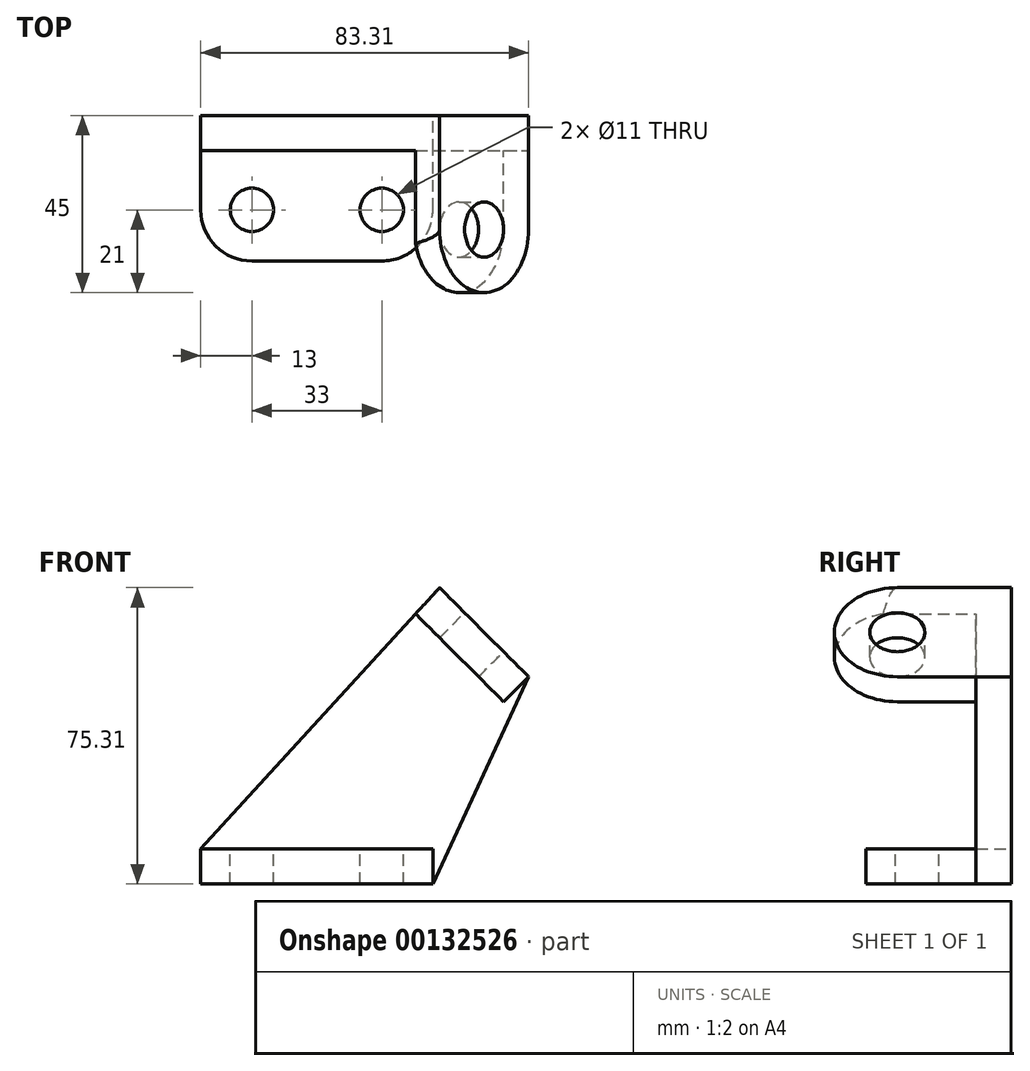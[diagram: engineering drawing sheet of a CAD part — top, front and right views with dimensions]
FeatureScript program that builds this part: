
annotation { "Feature Type Name" : "Feature", "Feature Type Description" : "" }
export const myFeature = defineFeature(function(context is Context, id is Id, definition is map)
    precondition{}
    {
        {
            var Q0;
            Q0=qCreatedBy(makeId("Front.planeOp"),FACE);
            var sketch = newSketch(context, id + "F0", { "sketchPlane" : qUnion([Q0])});
            skLineSegment(sketch, "E0.bottom", {"start": v(0, 0) * mm, "end": v(59, 0) * mm});
            skLineSegment(sketch, "E0.top", {"start": v(0, 9) * mm, "end": v(59, 9) * mm});
            skLineSegment(sketch, "E0.left", {"start": v(0, 0) * mm, "end": v(0, 9) * mm});
            skLineSegment(sketch, "E0.right", {"start": v(59, 0) * mm, "end": v(59, 9) * mm});
            skSolve(sketch);
        }
        {
            var Q0;
            Q0=makeQuery(id+"F0.imprint","IMPRINT",FACE,{"disambiguationData":[TD([[makeQuery(id+"F0.imprint","IMPRINT",EDGE,{"derivedFrom":sQuery(id+"F0.wireOp",EDGE,"E0.bottom")}),1.0]])]});
            extrude(context, id + "F1", {"entities" : qUnion([Q0]), "depth" : 37 * mm});
        }
        {
            var Q0;
            Q0=makeQuery(id+"F1.opExtrude","SWEPT_FACE",FACE,{"disambiguationData":[OSD([sQuery(id+"F0.wireOp",EDGE,"E0.top")])]});
            var sketch = newSketch(context, id + "F2", { "sketchPlane" : qUnion([Q0])});
            skCircle(sketch, "E1", {"center": v(46, -24) * mm, "radius": 5.5 * mm});
            skCircle(sketch, "E2", {"center": v(13, -24) * mm, "radius": 5.5 * mm});
            skSolve(sketch);
        }
        {
            var Q0;
            Q0 = qSketchRegion(id + "F2", true);
            var Q1;
            Q1=makeQuery(id+"F2.imprint","IMPRINT",FACE,{"disambiguationData":[TD([[makeQuery(id+"F2.imprint","IMPRINT",EDGE,{"derivedFrom":sQuery(id+"F2.wireOp",EDGE,"E2")}),1.0]])]});
            extrude(context, id + "F3", {"entities" : qUnion([Q0, Q1]), "operationType" : NewBodyOperationType.REMOVE, "oppositeDirection" : true, "depth" : 25 * mm});
        }
        {
            var Q0;
            Q0=makeQuery(id+"F1.opExtrude","CAP_FACE",FACE,{"disambiguationData":[OSD([sQuery(id+"F0.wireOp",EDGE,"E0.bottom"),sQuery(id+"F0.wireOp",EDGE,"E0.top"),sQuery(id+"F0.wireOp",EDGE,"E0.left"),sQuery(id+"F0.wireOp",EDGE,"E0.right")])],"isStart":true});
            var sketch = newSketch(context, id + "F4", { "sketchPlane" : qUnion([Q0])});
            skLineSegment(sketch, "E3", {"start": v(-59, 0) * mm, "end": v(-72, 0) * mm, "construction": true});
            skLineSegment(sketch, "E4", {"start": v(-72, 0) * mm, "end": v(-72, 80.83) * mm, "construction": true});
            skLineSegment(sketch, "E5", {"start": v(-61.08, 64) * mm, "end": v(-84.47, 64) * mm, "construction": true});
            skCircle(sketch, "E6", {"center": v(-72, 64) * mm, "radius": 1.23 * mm, "construction": true});
            skLineSegment(sketch, "E7", {"start": v(-72, 64) * mm, "end": v(-83.31, 52.69) * mm});
            skLineSegment(sketch, "E8", {"start": v(-72, 64) * mm, "end": v(-60.69, 75.31) * mm});
            skLineSegment(sketch, "E9", {"start": v(-59, 0) * mm, "end": v(-83.31, 52.69) * mm});
            skLineSegment(sketch, "E10", {"start": v(0, 9) * mm, "end": v(-60.69, 75.31) * mm});
            skLineSegment(sketch, "E11", {"start": v(-60.69, 75.31) * mm, "end": v(-54.61, 68.67) * mm});
            skLineSegment(sketch, "E12", {"start": v(-83.31, 52.69) * mm, "end": v(-77.24, 46.05) * mm});
            skLineSegment(sketch, "E13", {"start": v(-54.61, 68.67) * mm, "end": v(-77.24, 46.05) * mm});
            skSolve(sketch);
        }
        {
            var Q0;
            Q0=makeQuery(id+"F4.imprint","IMPRINT",FACE,{"disambiguationData":[TD([[makeQuery(id+"F4.imprint","IMPRINT",EDGE,{"derivedFrom":sQuery(id+"F4.wireOp",EDGE,"E9")}),-1.0]])]});
            extrude(context, id + "F5", {"entities" : qUnion([Q0]), "operationType" : NewBodyOperationType.ADD, "oppositeDirection" : true, "depth" : 9 * mm});
        }
        {
            var Q0;
            Q0=makeQuery(id+"F4.imprint","IMPRINT",FACE,{"disambiguationData":[TD([[makeQuery(id+"F4.imprint","IMPRINT",EDGE,{"derivedFrom":sQuery(id+"F4.wireOp",EDGE,"E7")}),1.0]])]});
            extrude(context, id + "F6", {"entities" : qUnion([Q0]), "operationType" : NewBodyOperationType.ADD, "oppositeDirection" : true, "depth" : 45 * mm});
        }
        {
            var Q0;
            Q0=makeQuery(id+"F6.opExtrude","SWEPT_FACE",FACE,{"disambiguationData":[OSD([sQuery(id+"F4.wireOp",EDGE,"E7"),sQuery(id+"F4.wireOp",EDGE,"E8")])]});
            var sketch = newSketch(context, id + "F7", { "sketchPlane" : qUnion([Q0])});
            skCircle(sketch, "E14", {"center": v(-29, -5.66) * mm, "radius": 7 * mm});
            skPoint(sketch, "E14.centerSnap0", {"position": v(0, -5.66) * mm});
            skArc(sketch, "E15", {"start": v(-29, 10.34) * mm, "mid": v(-45, -5.66) * mm, "end": v(-29, -21.66) * mm});
            skLineSegment(sketch, "E16", {"start": v(-29, -21.66) * mm, "end": v(0, -21.66) * mm});
            skLineSegment(sketch, "E17", {"start": v(-29, 10.34) * mm, "end": v(0, 10.34) * mm});
            skLineSegment(sketch, "E18", {"start": v(0, -21.66) * mm, "end": v(0, 10.34) * mm});
            skSolve(sketch);
        }
        {
            var Q0;
            Q0=makeQuery(id+"F7.imprint","IMPRINT",FACE,{"disambiguationData":[TD([[makeQuery(id+"F7.imprint","IMPRINT",EDGE,{"derivedFrom":sQuery(id+"F7.wireOp",EDGE,"E14")}),1.0]])]});
            var Q1;
            {var subQ0=sQuery(id+"F7.wireOp",EDGE,"E15");var subQ1=sQuery(id+"F4.wireOp",EDGE,"E8");var subQ2=makeQuery(id+"F6.opExtrude","SWEPT_EDGE",EDGE,{"disambiguationData":[OSD([subQ1,sQuery(id+"F4.wireOp",EDGE,"E11")])]});var subQ3=makeQuery(id+"F7.imprint","INTERSECT",VERTEX,{"derivedFrom":[subQ2,subQ0]});Q1=makeQuery(id+"F7.imprint","IMPRINT",FACE,{"disambiguationData":[TD([[makeQuery(id+"F7.imprint","IMPRINT",EDGE,{"disambiguationData":[TD([[subQ3,-1.0]])],"derivedFrom":subQ0}),-1.0]])]});}
            var Q2;
            {var subQ0=sQuery(id+"F7.wireOp",EDGE,"E15");var subQ1=sQuery(id+"F4.wireOp",EDGE,"E7");var subQ4=makeQuery(id+"F6.opExtrude","CAP_EDGE",EDGE,{"disambiguationData":[OSD([subQ1,sQuery(id+"F4.wireOp",EDGE,"E8")])],"isStart":false});var subQ5=makeQuery(id+"F7.imprint","INTERSECT",VERTEX,{"derivedFrom":[subQ4,subQ0]});Q2=makeQuery(id+"F7.imprint","IMPRINT",FACE,{"disambiguationData":[TD([[makeQuery(id+"F7.imprint","IMPRINT",EDGE,{"disambiguationData":[TD([[subQ5,-1.0]])],"derivedFrom":subQ0}),-1.0]])]});}
            var Q3;
            Q3=makeQuery(id+"F6.opExtrude","SWEPT_FACE",FACE,{"disambiguationData":[OSD([sQuery(id+"F4.wireOp",EDGE,"E12")])]});
            extrude(context, id + "F8", {"entities" : qUnion([Q0, Q1, Q2, Q3]), "operationType" : NewBodyOperationType.REMOVE, "oppositeDirection" : true, "depth" : 25 * mm});
        }
        {
            var Q0;
            Q0=makeQuery(id+"F1.opExtrude","CAP_EDGE",EDGE,{"disambiguationData":[OSD([sQuery(id+"F0.wireOp",EDGE,"E0.right")])],"isStart":false});
            var Q1;
            Q1=makeQuery(id+"F1.opExtrude","CAP_EDGE",EDGE,{"disambiguationData":[OSD([sQuery(id+"F0.wireOp",EDGE,"E0.left")])],"isStart":false});
            fillet(context, id + "F9", {"entities" : qUnion([Q0, Q1]), "radius" : 13 * mm, "tangentPropagation" : true, "allowEdgeOverflow" : false});
        }
    });
